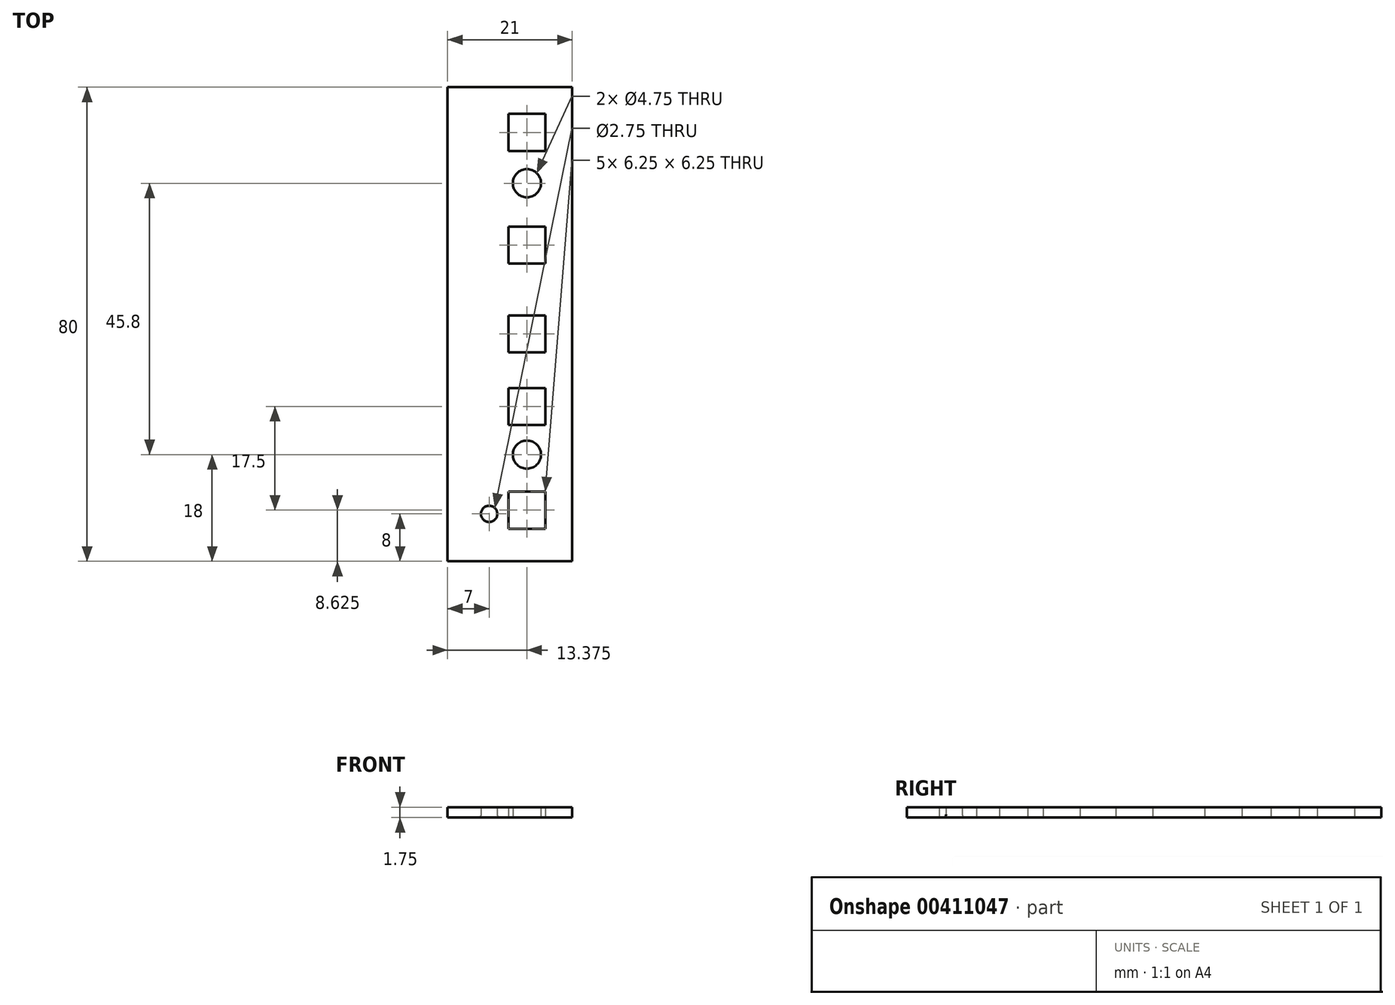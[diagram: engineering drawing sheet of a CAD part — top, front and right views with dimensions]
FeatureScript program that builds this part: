
annotation { "Feature Type Name" : "Feature", "Feature Type Description" : "" }
export const myFeature = defineFeature(function(context is Context, id is Id, definition is map)
    precondition{}
    {
        {
            var Q0;
            Q0=qCreatedBy(makeId("Top.planeOp"),FACE);
            var sketch = newSketch(context, id + "F0", { "sketchPlane" : qUnion([Q0])});
            skLineSegment(sketch, "E0.bottom", {"start": v(-8, -38) * mm, "end": v(8, -38) * mm});
            skLineSegment(sketch, "E0.top", {"start": v(-8, 38) * mm, "end": v(8, 38) * mm});
            skLineSegment(sketch, "E0.left", {"start": v(-8, -38) * mm, "end": v(-8, 38) * mm});
            skLineSegment(sketch, "E0.right", {"start": v(8, -38) * mm, "end": v(8, 38) * mm});
            skPoint(sketch, "E0.middle", {"position": v(0, 0) * mm});
            skLineSegment(sketch, "E1", {"start": v(2.41, 38) * mm, "end": v(2.41, 35.5) * mm});
            skLineSegment(sketch, "E2", {"start": v(8, 34.82) * mm, "end": v(6, 34.82) * mm});
            skLineSegment(sketch, "E3", {"start": v(6, 34.82) * mm, "end": v(-0.25, 34.82) * mm});
            skLineSegment(sketch, "E4", {"start": v(2.41, 35.5) * mm, "end": v(2.41, 29.25) * mm});
            skLineSegment(sketch, "E5", {"start": v(-0.25, 34.82) * mm, "end": v(-0.25, 29.25) * mm});
            skLineSegment(sketch, "E6", {"start": v(-0.25, 29.25) * mm, "end": v(2.41, 29.25) * mm});
            skLineSegment(sketch, "E7", {"start": v(6, 34.82) * mm, "end": v(6, 29.25) * mm});
            skLineSegment(sketch, "E8", {"start": v(6, 29.25) * mm, "end": v(2.41, 29.25) * mm});
            skLineSegment(sketch, "E9", {"start": v(2.41, 35.5) * mm, "end": v(-0.25, 35.5) * mm});
            skLineSegment(sketch, "E10", {"start": v(-0.25, 35.5) * mm, "end": v(-0.25, 34.82) * mm});
            skLineSegment(sketch, "E11", {"start": v(2.41, 35.5) * mm, "end": v(6, 35.5) * mm});
            skLineSegment(sketch, "E12", {"start": v(6, 35.5) * mm, "end": v(6, 34.82) * mm});
            skLineSegment(sketch, "E13", {"start": v(6, 36.73) * mm, "end": v(2.87, 36.73) * mm});
            skLineSegment(sketch, "E14", {"start": v(2.87, 38) * mm, "end": v(2.87, 13.37) * mm});
            skPoint(sketch, "E14.endSnap0", {"position": v(2.87, 34.82) * mm});
            skLineSegment(sketch, "E15.bottom", {"start": v(-0.25, 10.25) * mm, "end": v(6, 10.25) * mm});
            skLineSegment(sketch, "E15.top", {"start": v(-0.25, 16.5) * mm, "end": v(6, 16.5) * mm});
            skLineSegment(sketch, "E15.left", {"start": v(-0.25, 10.25) * mm, "end": v(-0.25, 16.5) * mm});
            skLineSegment(sketch, "E15.right", {"start": v(6, 10.25) * mm, "end": v(6, 16.5) * mm});
            skPoint(sketch, "E15.middle", {"position": v(2.87, 13.37) * mm});
            skLineSegment(sketch, "E16", {"start": v(2.87, 38) * mm, "end": v(2.87, -1.63) * mm});
            skLineSegment(sketch, "E17.bottom", {"start": v(6, -4.75) * mm, "end": v(-0.25, -4.75) * mm});
            skLineSegment(sketch, "E17.top", {"start": v(6, 1.5) * mm, "end": v(-0.25, 1.5) * mm});
            skLineSegment(sketch, "E17.left", {"start": v(6, -4.75) * mm, "end": v(6, 1.5) * mm});
            skLineSegment(sketch, "E17.right", {"start": v(-0.25, -4.75) * mm, "end": v(-0.25, 1.5) * mm});
            skPoint(sketch, "E17.middle", {"position": v(2.87, -1.63) * mm});
            skLineSegment(sketch, "E18", {"start": v(2.88, -38) * mm, "end": v(2.88, -13.87) * mm});
            skPoint(sketch, "E18.startSnap0", {"position": v(2.88, -4.75) * mm});
            skLineSegment(sketch, "E19.bottom", {"start": v(-0.25, -17) * mm, "end": v(6, -17) * mm});
            skLineSegment(sketch, "E19.top", {"start": v(-0.25, -10.75) * mm, "end": v(6, -10.75) * mm});
            skLineSegment(sketch, "E19.left", {"start": v(-0.25, -17) * mm, "end": v(-0.25, -10.75) * mm});
            skLineSegment(sketch, "E19.right", {"start": v(6, -17) * mm, "end": v(6, -10.75) * mm});
            skPoint(sketch, "E19.middle", {"position": v(2.88, -13.87) * mm});
            skLineSegment(sketch, "E20", {"start": v(2.88, -38) * mm, "end": v(2.88, -31.38) * mm});
            skLineSegment(sketch, "E21.bottom", {"start": v(-0.25, -34.5) * mm, "end": v(6, -34.5) * mm});
            skLineSegment(sketch, "E21.top", {"start": v(-0.25, -28.25) * mm, "end": v(6, -28.25) * mm});
            skLineSegment(sketch, "E21.left", {"start": v(-0.25, -34.5) * mm, "end": v(-0.25, -28.25) * mm});
            skLineSegment(sketch, "E21.right", {"start": v(6, -34.5) * mm, "end": v(6, -28.25) * mm});
            skPoint(sketch, "E21.middle", {"position": v(2.88, -31.38) * mm});
            skLineSegment(sketch, "E22", {"start": v(8, -25.28) * mm, "end": v(-3.5, -25.28) * mm});
            skLineSegment(sketch, "E23", {"start": v(-3.5, -38) * mm, "end": v(-3.5, -32) * mm});
            skCircle(sketch, "E24", {"center": v(-3.5, -32) * mm, "radius": 1.38 * mm});
            skLineSegment(sketch, "E25", {"start": v(2.87, 38) * mm, "end": v(2.87, 23.8) * mm});
            skCircle(sketch, "E26", {"center": v(2.87, 23.8) * mm, "radius": 2.38 * mm});
            skLineSegment(sketch, "E27", {"start": v(2.88, -38) * mm, "end": v(2.88, -22) * mm});
            skCircle(sketch, "E28", {"center": v(2.88, -22) * mm, "radius": 2.38 * mm});
            skLineSegment(sketch, "E29.bottom", {"start": v(-10.5, -40) * mm, "end": v(10.5, -40) * mm});
            skLineSegment(sketch, "E29.top", {"start": v(-10.5, 40) * mm, "end": v(10.5, 40) * mm});
            skLineSegment(sketch, "E29.left", {"start": v(-10.5, -40) * mm, "end": v(-10.5, 40) * mm});
            skLineSegment(sketch, "E29.right", {"start": v(10.5, -40) * mm, "end": v(10.5, 40) * mm});
            skSolve(sketch);
        }
        {
            var Q0;
            Q0 = qSketchRegion(id + "F0", true);
            var Q1;
            {var subQ19=sQuery(id+"F0.wireOp",EDGE,"E0.left");Q1=makeQuery(id+"F0.imprint","IMPRINT",FACE,{"disambiguationData":[TD([[makeQuery(id+"F0.imprint","IMPRINT",EDGE,{"derivedFrom":subQ19}),-1.0]])]});}
            var Q2;
            {var subQ0=sQuery(id+"F0.wireOp",EDGE,"E21.right");Q2=makeQuery(id+"F0.imprint","IMPRINT",FACE,{"disambiguationData":[TD([[makeQuery(id+"F0.imprint","IMPRINT",EDGE,{"derivedFrom":subQ0}),-1.0]])]});}
            var Q3;
            {var subQ0=sQuery(id+"F0.wireOp",EDGE,"E2");Q3=makeQuery(id+"F0.imprint","IMPRINT",FACE,{"disambiguationData":[TD([[makeQuery(id+"F0.imprint","IMPRINT",EDGE,{"derivedFrom":subQ0}),-1.0]])]});}
            var Q4;
            {var subQ4=sQuery(id+"F0.wireOp",EDGE,"E1");Q4=makeQuery(id+"F0.imprint","IMPRINT",FACE,{"disambiguationData":[TD([[makeQuery(id+"F0.imprint","IMPRINT",EDGE,{"derivedFrom":subQ4}),1.0]])]});}
            extrude(context, id + "F1", {"entities" : qUnion([Q0, Q1, Q2, Q3, Q4]), "depth" : 1.75 * mm});
        }
        {
            var Q0;
            Q0=makeQuery(id+"F1.opExtrude","CAP_EDGE",EDGE,{"disambiguationData":[OSD([sQuery(id+"F0.wireOp",EDGE,"E24")])],"isStart":true});
            fillet(context, id + "F2", {"entities" : qUnion([Q0]), "radius" : 0.5 * mm, "tangentPropagation" : true, "allowEdgeOverflow" : false});
        }
    });
